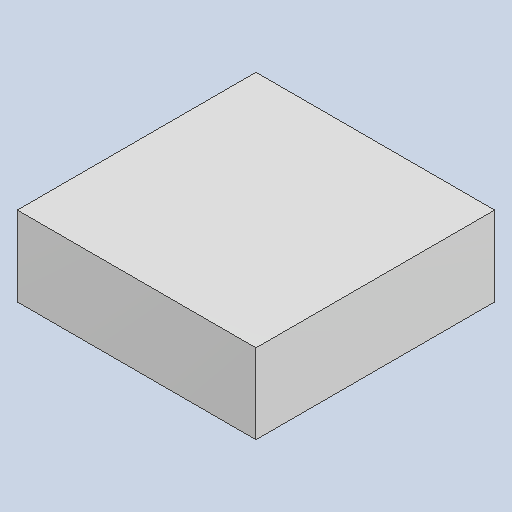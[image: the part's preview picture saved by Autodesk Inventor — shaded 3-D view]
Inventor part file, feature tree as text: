
AUTODESK INVENTOR PART (.ipt)
format: ipt  version: 2023.4 (Build 274418000, 418)  size: 79,872 bytes
history: native  units: mm
features: extrude x1
ambient origin geometry x8: Origin, YZ Plane, XZ Plane, XY Plane, X Axis, Y Axis, Z Axis, Center Point
bodies: Solid1 (feature_tree)
feature tree (1):
  extrude  "Extruded_6"  [1 undecoded]
note: 1 required parameter value undecoded (feature->parameter linkage not recoverable at this tier; creation-order binding heuristic only, values carry confidence <= 0.55)
